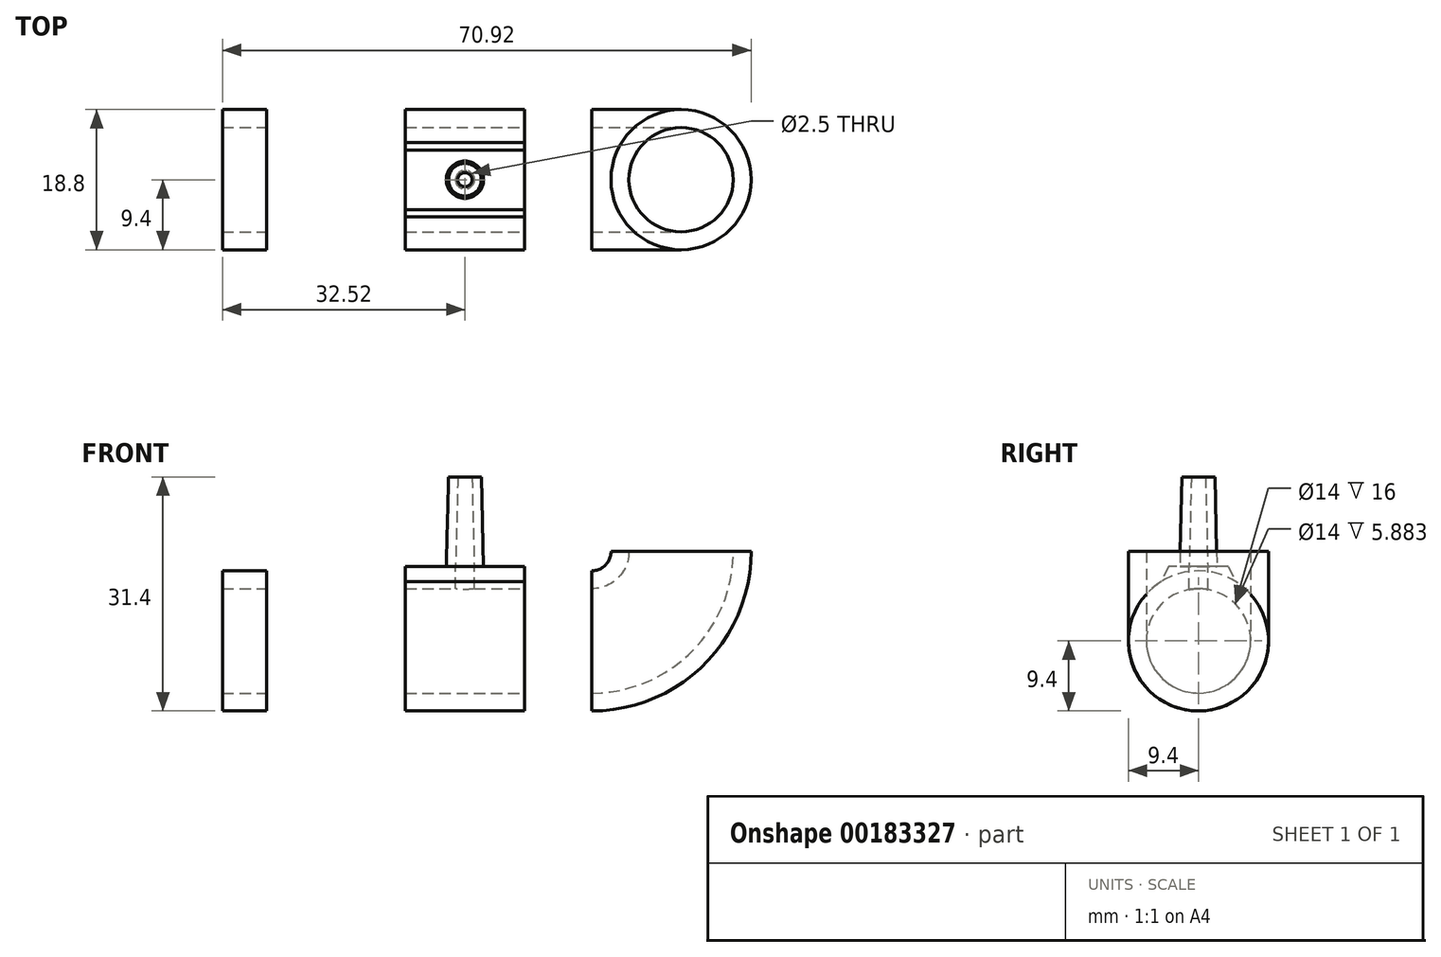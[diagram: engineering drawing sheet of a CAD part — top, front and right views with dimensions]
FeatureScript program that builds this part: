
annotation { "Feature Type Name" : "Feature", "Feature Type Description" : "" }
export const myFeature = defineFeature(function(context is Context, id is Id, definition is map)
    precondition{}
    {
        {
            var Q0;
            Q0=qCreatedBy(makeId("Front.planeOp"),FACE);
            var sketch = newSketch(context, id + "F0", { "sketchPlane" : qUnion([Q0])});
            skArc(sketch, "E0", {"start": v(-37, 0) * mm, "mid": v(-33.49, -8.49) * mm, "end": v(-25, -12) * mm});
            skLineSegment(sketch, "E1", {"start": v(-25, -12) * mm, "end": v(25, -12) * mm});
            skArc(sketch, "E2", {"start": v(25, -12) * mm, "mid": v(33.49, -8.49) * mm, "end": v(37, 0) * mm});
            skLineSegment(sketch, "E3", {"start": v(-25, 0) * mm, "end": v(25, 0) * mm, "construction": true});
            skSolve(sketch);
        }
        {
            var Q0;
            Q0=qCreatedBy(makeId("Top.planeOp"),FACE);
            var sketch = newSketch(context, id + "F1", { "sketchPlane" : qUnion([Q0])});
            skCircle(sketch, "E4", {"center": v(-37, 0) * mm, "radius": 9.4 * mm});
            skCircle(sketch, "E5", {"center": v(-37, 0) * mm, "radius": 7 * mm});
            skSolve(sketch);
        }
        {
            var Q0;
            Q0=makeQuery(id+"F1.imprint","IMPRINT",FACE,{"disambiguationData":[TD([[makeQuery(id+"F1.imprint","IMPRINT",EDGE,{"derivedFrom":sQuery(id+"F1.wireOp",EDGE,"E4")}),1.0]])]});
            var Q1;
            Q1 = qConstructionFilter(qBodyType(qCreatedBy(id + "F0" ,EDGE), BodyType.WIRE), ConstructionObject.NO);
            sweep(context, id + "F2", {"profiles" : qUnion([Q0]), "path" : qUnion([Q1])});
        }
        {
            var Q0;
            Q0=qCreatedBy(makeId("Right.planeOp"),FACE);
            var sketch = newSketch(context, id + "F3", { "sketchPlane" : qUnion([Q0])});
            skArc(sketch, "E6", {"start": v(7.18, -8.47) * mm, "mid": v(0, -4) * mm, "end": v(-7.18, -8.47) * mm});
            skLineSegment(sketch, "E7", {"start": v(0, -2) * mm, "end": v(-4, -2) * mm});
            skLineSegment(sketch, "E8", {"start": v(-4, -2) * mm, "end": v(-7.18, -8.47) * mm});
            skLineSegment(sketch, "E9", {"start": v(0, -2) * mm, "end": v(4, -2) * mm});
            skLineSegment(sketch, "E10", {"start": v(4, -2) * mm, "end": v(7.18, -8.47) * mm});
            skSolve(sketch);
        }
        {
            var Q0;
            Q0 = qSketchRegion(id + "F3", true);
            var Q1;
            Q1=sQuery(id+"F0.wireOp",VERTEX,"E2.start");
            extrude(context, id + "F4", {"entities" : qUnion([Q0]), "operationType" : NewBodyOperationType.ADD, "endBound" : BoundingType.SYMMETRIC, "endBoundEntityVertex" : qUnion([Q1]), "depth" : 36.6 * mm});
        }
        {
            var Q0;
            Q0=qCreatedBy(makeId("Front.planeOp"),FACE);
            var sketch = newSketch(context, id + "F5", { "sketchPlane" : qUnion([Q0])});
            skLineSegment(sketch, "E11", {"start": v(5.5, -2) * mm, "end": v(5.8, 10) * mm});
            skLineSegment(sketch, "E12", {"start": v(5.8, 10) * mm, "end": v(7.05, 10) * mm});
            skLineSegment(sketch, "E13", {"start": v(7.05, 10) * mm, "end": v(6.75, -2) * mm});
            skLineSegment(sketch, "E14", {"start": v(6.75, -2) * mm, "end": v(5.5, -2) * mm});
            skLineSegment(sketch, "E15", {"start": v(8, -2) * mm, "end": v(8, 10) * mm, "construction": true});
            skLineSegment(sketch, "E16", {"start": v(5.5, -2) * mm, "end": v(0, -2) * mm, "construction": true});
            skLineSegment(sketch, "E17", {"start": v(6.75, -2) * mm, "end": v(8, -2) * mm});
            skLineSegment(sketch, "E18.top", {"start": v(6.75, -12) * mm, "end": v(8, -12) * mm});
            skLineSegment(sketch, "E18.left", {"start": v(6.75, -2) * mm, "end": v(6.75, -12) * mm});
            skLineSegment(sketch, "E18.right", {"start": v(8, -2) * mm, "end": v(8, -12) * mm});
            skSolve(sketch);
        }
        {
            var Q0;
            Q0=makeQuery(id+"F5.imprint","IMPRINT",FACE,{"disambiguationData":[TD([[makeQuery(id+"F5.imprint","IMPRINT",EDGE,{"derivedFrom":sQuery(id+"F5.wireOp",EDGE,"E11")}),-1.0]])]});
            var Q1;
            Q1=sQuery(id+"F5.wireOp",EDGE,"E15");
            revolve(context, id + "F6", {"operationType" : NewBodyOperationType.ADD, "entities" : qUnion([Q0]), "axis" : qUnion([Q1]), "revolveType" : RevolveType.FULL});
        }
        {
            var Q0;
            Q0=makeQuery(id+"F5.imprint","IMPRINT",FACE,{"disambiguationData":[TD([[makeQuery(id+"F5.imprint","IMPRINT",EDGE,{"derivedFrom":sQuery(id+"F5.wireOp",EDGE,"E17")}),-1.0]])]});
            var Q1;
            Q1=sQuery(id+"F5.wireOp",EDGE,"E15");
            revolve(context, id + "F7", {"operationType" : NewBodyOperationType.REMOVE, "entities" : qUnion([Q0]), "axis" : qUnion([Q1]), "revolveType" : RevolveType.FULL, "oppositeDirection" : true});
        }
        {
            var Q0;
            Q0=qCreatedBy(makeId("Front.planeOp"),FACE);
            var sketch = newSketch(context, id + "F8", { "sketchPlane" : qUnion([Q0])});
            skLineSegment(sketch, "E19.bottom", {"start": v(0, 17.47) * mm, "end": v(16, 17.47) * mm});
            skLineSegment(sketch, "E19.top", {"start": v(0, -28.92) * mm, "end": v(16, -28.92) * mm});
            skLineSegment(sketch, "E19.left", {"start": v(0, 17.47) * mm, "end": v(0, -28.92) * mm});
            skLineSegment(sketch, "E19.right", {"start": v(16, 17.47) * mm, "end": v(16, -28.92) * mm});
            skLineSegment(sketch, "E20.bottom", {"start": v(25, 17.46) * mm, "end": v(48.17, 17.46) * mm});
            skLineSegment(sketch, "E20.top", {"start": v(25, -30.47) * mm, "end": v(48.17, -30.47) * mm});
            skLineSegment(sketch, "E20.left", {"start": v(25, 17.46) * mm, "end": v(25, -30.47) * mm});
            skLineSegment(sketch, "E20.right", {"start": v(48.17, 17.46) * mm, "end": v(48.17, -30.47) * mm});
            skLineSegment(sketch, "E21.bottom", {"start": v(-18.64, 17.66) * mm, "end": v(-24.52, 17.66) * mm});
            skLineSegment(sketch, "E21.top", {"start": v(-18.64, -32.44) * mm, "end": v(-24.52, -32.44) * mm});
            skLineSegment(sketch, "E21.left", {"start": v(-18.64, 17.66) * mm, "end": v(-18.64, -32.44) * mm});
            skLineSegment(sketch, "E21.right", {"start": v(-24.52, 17.66) * mm, "end": v(-24.52, -32.44) * mm});
            skSolve(sketch);
        }
        {
            var Q0;
            Q0 = qSketchRegion(id + "F8", true);
            extrude(context, id + "F9", {"entities" : qUnion([Q0]), "operationType" : NewBodyOperationType.INTERSECT, "endBound" : BoundingType.SYMMETRIC, "depth" : 25 * mm});
        }
    });
